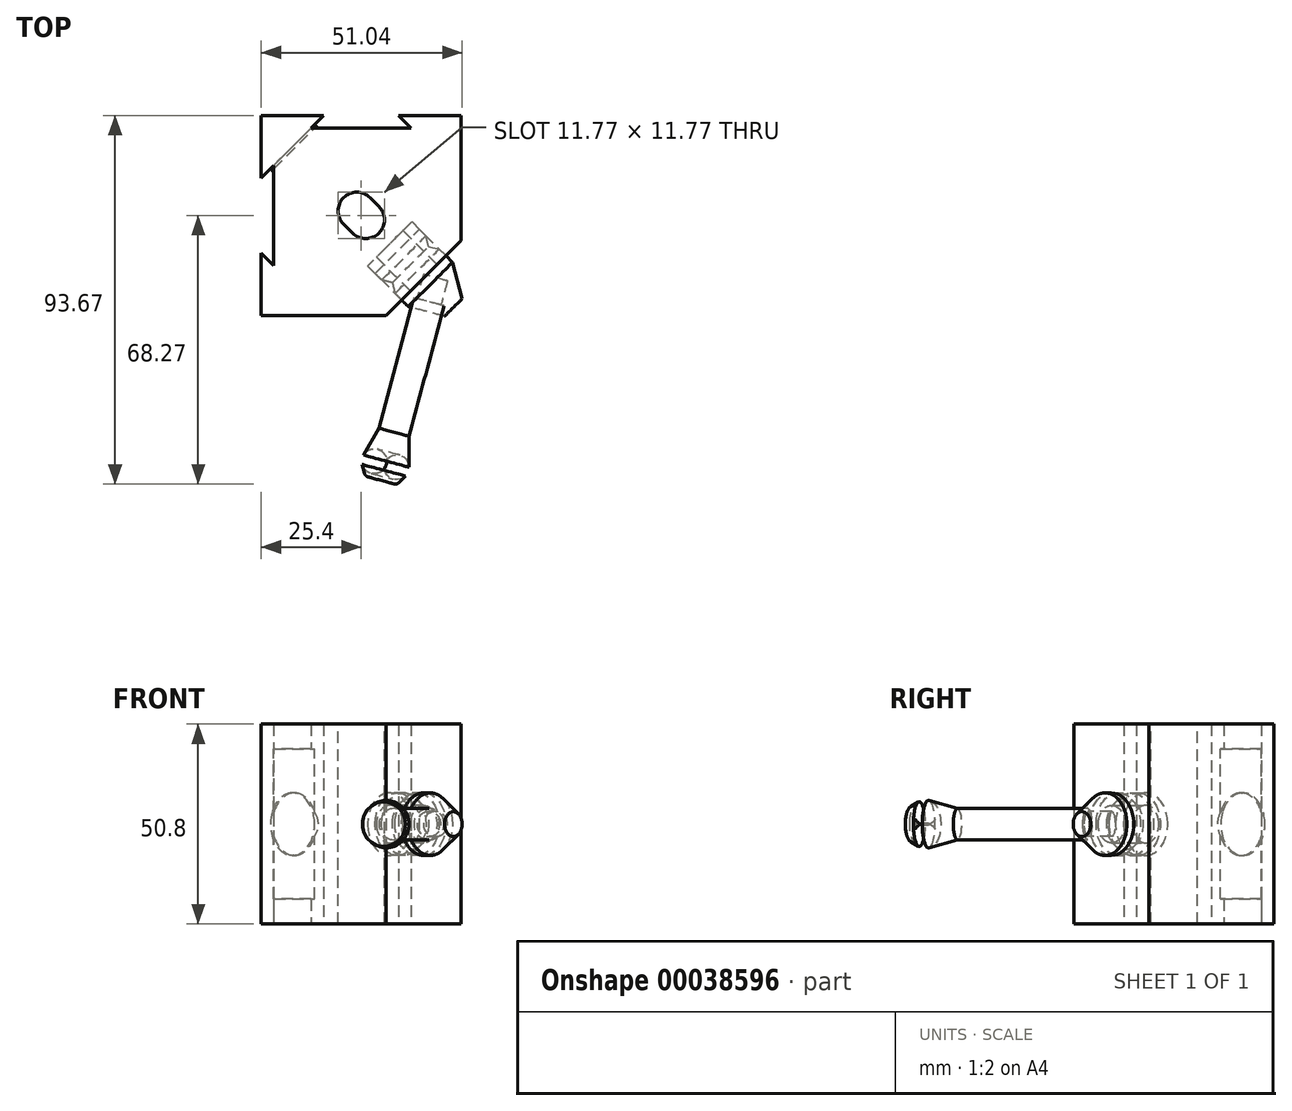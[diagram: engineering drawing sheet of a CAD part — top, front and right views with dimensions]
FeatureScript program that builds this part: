
annotation { "Feature Type Name" : "Feature", "Feature Type Description" : "" }
export const myFeature = defineFeature(function(context is Context, id is Id, definition is map)
    precondition{}
    {
        {
            var Q0;
            Q0=qCreatedBy(makeId("Top.planeOp"),FACE);
            var sketch = newSketch(context, id + "F0", { "sketchPlane" : qUnion([Q0])});
            skLineSegment(sketch, "E0", {"start": v(-64.42, 64.42) * mm, "end": v(64.42, -64.42) * mm, "construction": true});
            skPoint(sketch, "E1", {"position": v(0, 0) * mm});
            skLineSegment(sketch, "E2", {"start": v(0, 69.1) * mm, "end": v(0, -69.1) * mm, "construction": true});
            skLineSegment(sketch, "E3", {"start": v(38.45, 38.45) * mm, "end": v(-38.45, -38.45) * mm, "construction": true});
            skSolve(sketch);
        }
        {
            var Q0;
            Q0=qCreatedBy(makeId("Top.planeOp"),FACE);
            var sketch = newSketch(context, id + "F1", { "sketchPlane" : qUnion([Q0])});
            skLineSegment(sketch, "E4.rect.bottom", {"start": v(25.4, 25.4) * mm, "end": v(-25.4, 25.4) * mm});
            skLineSegment(sketch, "E4.rect.top", {"start": v(25.4, -25.4) * mm, "end": v(-25.4, -25.4) * mm});
            skLineSegment(sketch, "E4.rect.left", {"start": v(25.4, 25.4) * mm, "end": v(25.4, -25.4) * mm});
            skLineSegment(sketch, "E4.rect.right", {"start": v(-25.4, 25.4) * mm, "end": v(-25.4, -25.4) * mm});
            skPoint(sketch, "E4.rect.middle", {"position": v(0, 0) * mm});
            skLineSegment(sketch, "E5", {"start": v(-9.52, 25.4) * mm, "end": v(-12.7, 22.22) * mm});
            skLineSegment(sketch, "E6", {"start": v(-12.7, 22.22) * mm, "end": v(12.7, 22.22) * mm});
            skLineSegment(sketch, "E7", {"start": v(12.7, 22.22) * mm, "end": v(9.52, 25.4) * mm});
            skLineSegment(sketch, "E8", {"start": v(-25.4, 9.52) * mm, "end": v(-22.22, 12.7) * mm});
            skLineSegment(sketch, "E9", {"start": v(-22.22, 12.7) * mm, "end": v(-22.22, -12.7) * mm});
            skLineSegment(sketch, "E10", {"start": v(-25.4, -9.52) * mm, "end": v(-22.22, -12.7) * mm});
            skLineSegment(sketch, "E11", {"start": v(-22.22, 11.8) * mm, "end": v(-11.8, 22.22) * mm});
            skLineSegment(sketch, "E12", {"start": v(6.35, -25.4) * mm, "end": v(25.4, -6.35) * mm});
            skLineSegment(sketch, "E13", {"start": v(-12.7, 22.22) * mm, "end": v(-22.22, 12.7) * mm});
            skCircle(sketch, "E14", {"center": v(0, 0) * mm, "radius": 4.76 * mm});
            skSolve(sketch);
        }
        {
            var Q0;
            {var subQ0=sQuery(id+"F1.wireOp",EDGE,"E11");Q0=makeQuery(id+"F1.imprint","IMPRINT",FACE,{"disambiguationData":[TD([[makeQuery(id+"F1.imprint","IMPRINT",EDGE,{"derivedFrom":subQ0}),1.0]])]});}
            var Q1;
            {var subQ2=sQuery(id+"F1.wireOp",EDGE,"E7");Q1=makeQuery(id+"F1.imprint","IMPRINT",FACE,{"disambiguationData":[TD([[makeQuery(id+"F1.imprint","IMPRINT",EDGE,{"derivedFrom":subQ2}),-1.0]])]});}
            var Q2;
            {var subQ1=sQuery(id+"F1.wireOp",EDGE,"E5");Q2=makeQuery(id+"F1.imprint","IMPRINT",FACE,{"disambiguationData":[TD([[makeQuery(id+"F1.imprint","IMPRINT",EDGE,{"derivedFrom":subQ1}),-1.0]])]});}
            extrude(context, id + "F2", {"entities" : qUnion([Q0, Q1, Q2]), "endBound" : BoundingType.SYMMETRIC, "depth" : 50.8 * mm});
        }
        {
            var Q0;
            {var subQ1=sQuery(id+"F1.wireOp",EDGE,"E5");Q0=makeQuery(id+"F1.imprint","IMPRINT",FACE,{"disambiguationData":[TD([[makeQuery(id+"F1.imprint","IMPRINT",EDGE,{"derivedFrom":subQ1}),-1.0]])]});}
            var Q1;
            {var subQ0=sQuery(id+"F1.wireOp",EDGE,"E11");Q1=makeQuery(id+"F1.imprint","IMPRINT",FACE,{"disambiguationData":[TD([[makeQuery(id+"F1.imprint","IMPRINT",EDGE,{"derivedFrom":subQ0}),1.0]])]});}
            extrude(context, id + "F3", {"entities" : qUnion([Q0, Q1]), "operationType" : NewBodyOperationType.REMOVE, "endBound" : BoundingType.SYMMETRIC, "oppositeDirection" : true, "depth" : 38.1 * mm});
        }
        {
            var Q0;
            {var subQ1=sQuery(id+"F1.wireOp",EDGE,"E5");Q0=makeQuery(id+"F1.imprint","IMPRINT",FACE,{"disambiguationData":[TD([[makeQuery(id+"F1.imprint","IMPRINT",EDGE,{"derivedFrom":subQ1}),-1.0]])]});}
            extrude(context, id + "F4", {"entities" : qUnion([Q0]), "endBound" : BoundingType.SYMMETRIC, "depth" : 38.1 * mm});
        }
        {
            var Q0;
            Q0=makeQuery(id+"F4.opExtrude","SWEPT_FACE",FACE,{"disambiguationData":[OSD([sQuery(id+"F1.wireOp",EDGE,"E5"),sQuery(id+"F1.wireOp",EDGE,"E8"),sQuery(id+"F1.wireOp",EDGE,"E13")])]});
            var sketch = newSketch(context, id + "F5", { "sketchPlane" : qUnion([Q0])});
            skCircle(sketch, "E15", {"center": v(0, 0) * mm, "radius": 7.94 * mm});
            skSolve(sketch);
        }
        {
            var Q0;
            Q0 = qSketchRegion(id + "F5", true);
            var Q1;
            Q1=makeQuery(id+"F2.opExtrude","SWEPT_FACE",FACE,{"disambiguationData":[OSD([sQuery(id+"F1.wireOp",EDGE,"E12")])]});
            extrude(context, id + "F6", {"entities" : qUnion([Q0]), "operationType" : NewBodyOperationType.REMOVE, "endBound" : BoundingType.UP_TO_SURFACE, "endBoundEntityFace" : qUnion([Q1]), "depth" : 25.4 * mm});
        }
        {
            var Q0;
            Q0 = qSketchRegion(id + "F5", true);
            extrude(context, id + "F7", {"entities" : qUnion([Q0]), "operationType" : NewBodyOperationType.ADD, "depth" : 34.92 * mm});
        }
        {
            var Q0;
            Q0=makeQuery(id+"F7.opExtrude","CAP_FACE",FACE,{"disambiguationData":[OSD([sQuery(id+"F5.wireOp",EDGE,"E15")])],"isStart":false});
            var sketch = newSketch(context, id + "F8", { "sketchPlane" : qUnion([Q0])});
            skCircle(sketch, "E16", {"center": v(0, 0) * mm, "radius": 4.76 * mm});
            skSolve(sketch);
        }
        {
            var Q0;
            Q0 = qSketchRegion(id + "F8", true);
            var Q1;
            Q1=makeQuery(id+"F2.opExtrude","SWEPT_FACE",FACE,{"disambiguationData":[OSD([sQuery(id+"F1.wireOp",EDGE,"E12")])]});
            extrude(context, id + "F9", {"entities" : qUnion([Q0]), "operationType" : NewBodyOperationType.ADD, "endBound" : BoundingType.UP_TO_SURFACE, "endBoundEntityFace" : qUnion([Q1]), "depth" : 12.7 * mm});
        }
        {
            var Q0;
            Q0=makeQuery(id+"F2.opExtrude","CAP_FACE",FACE,{"disambiguationData":[OSD([sQuery(id+"F1.wireOp",EDGE,"E4.rect.bottom"),sQuery(id+"F1.wireOp",EDGE,"E4.rect.top"),sQuery(id+"F1.wireOp",EDGE,"E4.rect.left"),sQuery(id+"F1.wireOp",EDGE,"E4.rect.right"),sQuery(id+"F1.wireOp",EDGE,"E5"),sQuery(id+"F1.wireOp",EDGE,"E6"),sQuery(id+"F1.wireOp",EDGE,"E7"),sQuery(id+"F1.wireOp",EDGE,"E8"),sQuery(id+"F1.wireOp",EDGE,"E9"),sQuery(id+"F1.wireOp",EDGE,"E10"),sQuery(id+"F1.wireOp",EDGE,"E12"),sQuery(id+"F1.wireOp",EDGE,"E14")])],"isStart":false});
            var sketch = newSketch(context, id + "F10", { "sketchPlane" : qUnion([Q0])});
            skArc(sketch, "E17", {"start": v(2.25, 4.5) * mm, "mid": v(-4.5, 4.5) * mm, "end": v(-4.5, -2.25) * mm});
            skArc(sketch, "E18", {"start": v(-2.25, -4.5) * mm, "mid": v(4.5, -4.5) * mm, "end": v(4.5, 2.25) * mm});
            skLineSegment(sketch, "E19", {"start": v(-4.5, -2.25) * mm, "end": v(-2.25, -4.5) * mm});
            skLineSegment(sketch, "E20", {"start": v(2.25, 4.5) * mm, "end": v(4.5, 2.25) * mm});
            skSolve(sketch);
        }
        {
            var Q0;
            Q0 = qSketchRegion(id + "F10", true);
            extrude(context, id + "F11", {"entities" : qUnion([Q0]), "operationType" : NewBodyOperationType.REMOVE, "endBound" : BoundingType.THROUGH_ALL, "oppositeDirection" : true, "depth" : 25.4 * mm});
        }
        {
            var Q0;
            Q0=qCreatedBy(makeId("Top.planeOp"),FACE);
            var sketch = newSketch(context, id + "F12", { "sketchPlane" : qUnion([Q0])});
            skLineSegment(sketch, "E21", {"start": v(9.14, -9.14) * mm, "end": v(3.53, -14.75) * mm});
            skLineSegment(sketch, "E22", {"start": v(3.53, -14.75) * mm, "end": v(5.21, -16.44) * mm});
            skLineSegment(sketch, "E23", {"start": v(5.21, -16.44) * mm, "end": v(6.22, -15.42) * mm});
            skLineSegment(sketch, "E24", {"start": v(6.22, -15.42) * mm, "end": v(9.6, -18.8) * mm});
            skLineSegment(sketch, "E25", {"start": v(9.6, -18.8) * mm, "end": v(8.58, -19.8) * mm});
            skLineSegment(sketch, "E26", {"start": v(8.58, -19.8) * mm, "end": v(11.95, -23.17) * mm});
            skLineSegment(sketch, "E27", {"start": v(11.95, -23.17) * mm, "end": v(21.15, -25.64) * mm});
            skLineSegment(sketch, "E28", {"start": v(21.15, -25.64) * mm, "end": v(23.4, -23.4) * mm});
            skLineSegment(sketch, "E29", {"start": v(23.4, -23.4) * mm, "end": v(9.14, -9.14) * mm});
            skLineSegment(sketch, "E30", {"start": v(12.5, -12.5) * mm, "end": v(6.66, -18.36) * mm, "construction": true});
            skLineSegment(sketch, "E31", {"start": v(5.21, -16.44) * mm, "end": v(7.9, -17.1) * mm});
            skLineSegment(sketch, "E32", {"start": v(7.9, -17.1) * mm, "end": v(8.58, -19.8) * mm});
            skSolve(sketch);
        }
        {
            var Q0;
            Q0 = qSketchRegion(id + "F12", true);
            var Q1;
            Q1=sQuery(id+"F0.wireOp",EDGE,"E0");
            revolve(context, id + "F13", {"entities" : qUnion([Q0]), "axis" : qUnion([Q1]), "revolveType" : RevolveType.FULL});
        }
        {
            var Q0;
            Q0=qCreatedBy(makeId("Top.planeOp"),FACE);
            var sketch = newSketch(context, id + "F14", { "sketchPlane" : qUnion([Q0])});
            skLineSegment(sketch, "E33", {"start": v(3.53, -72.98) * mm, "end": v(22.12, -3.61) * mm, "construction": true});
            skPoint(sketch, "E34", {"position": v(16.55, -24.4) * mm});
            skLineSegment(sketch, "E35", {"start": v(18.85, -15.82) * mm, "end": v(5.04, -67.34) * mm});
            skLineSegment(sketch, "E36", {"start": v(5.04, -67.34) * mm, "end": v(8.34, -68.22) * mm});
            skLineSegment(sketch, "E37", {"start": v(9.57, -67.9) * mm, "end": v(11.23, -66.23) * mm});
            skLineSegment(sketch, "E38", {"start": v(12.16, -63.98) * mm, "end": v(12.16, -56.1) * mm});
            skLineSegment(sketch, "E39", {"start": v(12.16, -56.1) * mm, "end": v(21.04, -22.98) * mm});
            skLineSegment(sketch, "E40", {"start": v(21.04, -22.98) * mm, "end": v(20.27, -22.77) * mm});
            skLineSegment(sketch, "E41", {"start": v(20.27, -22.77) * mm, "end": v(21.91, -16.64) * mm});
            skLineSegment(sketch, "E42", {"start": v(21.91, -16.64) * mm, "end": v(18.85, -15.82) * mm});
            skPoint(sketch, "E43.visualSharp", {"position": v(12.16, -65.3) * mm});
            skArc(sketch, "E43.filletArc", {"start": v(11.23, -66.23) * mm, "mid": v(11.92, -65.2) * mm, "end": v(12.16, -63.98) * mm});
            skPoint(sketch, "E44.visualSharp", {"position": v(9.05, -68.41) * mm});
            skArc(sketch, "E44.filletArc", {"start": v(8.34, -68.22) * mm, "mid": v(9, -68.22) * mm, "end": v(9.57, -67.9) * mm});
            skSolve(sketch);
        }
        {
            var Q0;
            Q0 = qSketchRegion(id + "F14", true);
            var Q1;
            Q1=sQuery(id+"F14.wireOp",EDGE,"E33");
            revolve(context, id + "F15", {"entities" : qUnion([Q0]), "axis" : qUnion([Q1]), "revolveType" : RevolveType.FULL});
        }
    });
